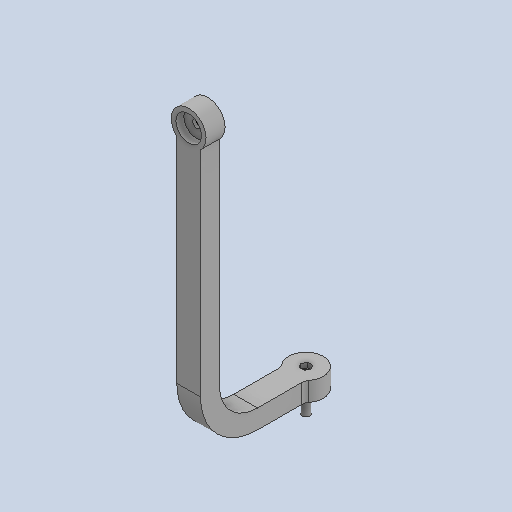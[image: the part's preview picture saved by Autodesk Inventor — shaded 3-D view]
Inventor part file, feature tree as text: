
AUTODESK INVENTOR PART (.ipt)
format: ipt  version: 2024 (Build 280153000, 153)  size: 332,800 bytes
history: native  units: mm
features: sketch x9, extrude x7, other x3, sweep x1, plane x1, mirror x1
ambient origin geometry x8: Origin, YZ Plane, XZ Plane, XY Plane, X Axis, Y Axis, Z Axis, Center Point
bodies: Solid1 (feature_tree)
feature tree (22):
  extrude  "Extrusion1"  Depth=12.0mm TaperAngle=0.0deg
  sweep  "Sweep2"
  plane  "Work Plane11"
  extrude  "Extrusion17"  TaperAngle=90.0deg  [1 undecoded]
  extrude  "Extrusion18"  TaperAngle=0.0deg  [1 undecoded]
  other  "Work Point1"
  extrude  "Extrusion20"  Depth=12.0mm TaperAngle=0.0deg
  extrude  "Extrusion22"  TaperAngle=0.0deg  [1 undecoded]
  mirror  "Mirror2"
  extrude  "Extrusion23"  Depth=10.0mm
  extrude  "Extrusion24"  Depth=26.0mm TaperAngle=0.0deg
  sketch  "Sketch1"  dims[d0=22.0mm d1=12.0mm d2=0.0mm]
  sketch  "Sketch22"  dims[d109=5.0mm d110=50.0mm]
  sketch  "Sketch23"  dims[d111=161.223987mm d112=90.0deg]
  sketch  "Sketch24"  dims[d113=30.0mm d114=0.0mm d115=0.0mm]
  sketch  "Sketch25"  dims[d116=-6.0mm d121=12.0mm d122=0.0mm]
  other  "Work Axis1"
  other  "Work Axis2"
  sketch  "Sketch27"  dims[d123=5.0mm d124=0.0mm d125=0.0mm]
  sketch  "Sketch29"  dims[d129=15.0mm d131=10.0mm]
  sketch  "Sketch30"  dims[d136=4.8mm d137=26.0mm d138=0.0mm]
  sketch  "Sketch31"  dims[d142=22.0mm d143=12.0mm d144=16.2mm d145=5.0mm d146=0.0mm d148=5.5mm d149=3.0mm d150=0.0mm d151=3.2mm d152=0.0mm d153=0.0mm d74=0.5mm d75=0.872665mm d76=0.5mm d77=0.872665mm d98=0.0mm d99=0.0mm d100=0.0mm d101=0.0mm d102=0.872665mm d103=0.5mm d104=0.872665mm]
note: 3 required parameter values undecoded (feature->parameter linkage not recoverable at this tier; creation-order binding heuristic only, values carry confidence <= 0.55)
